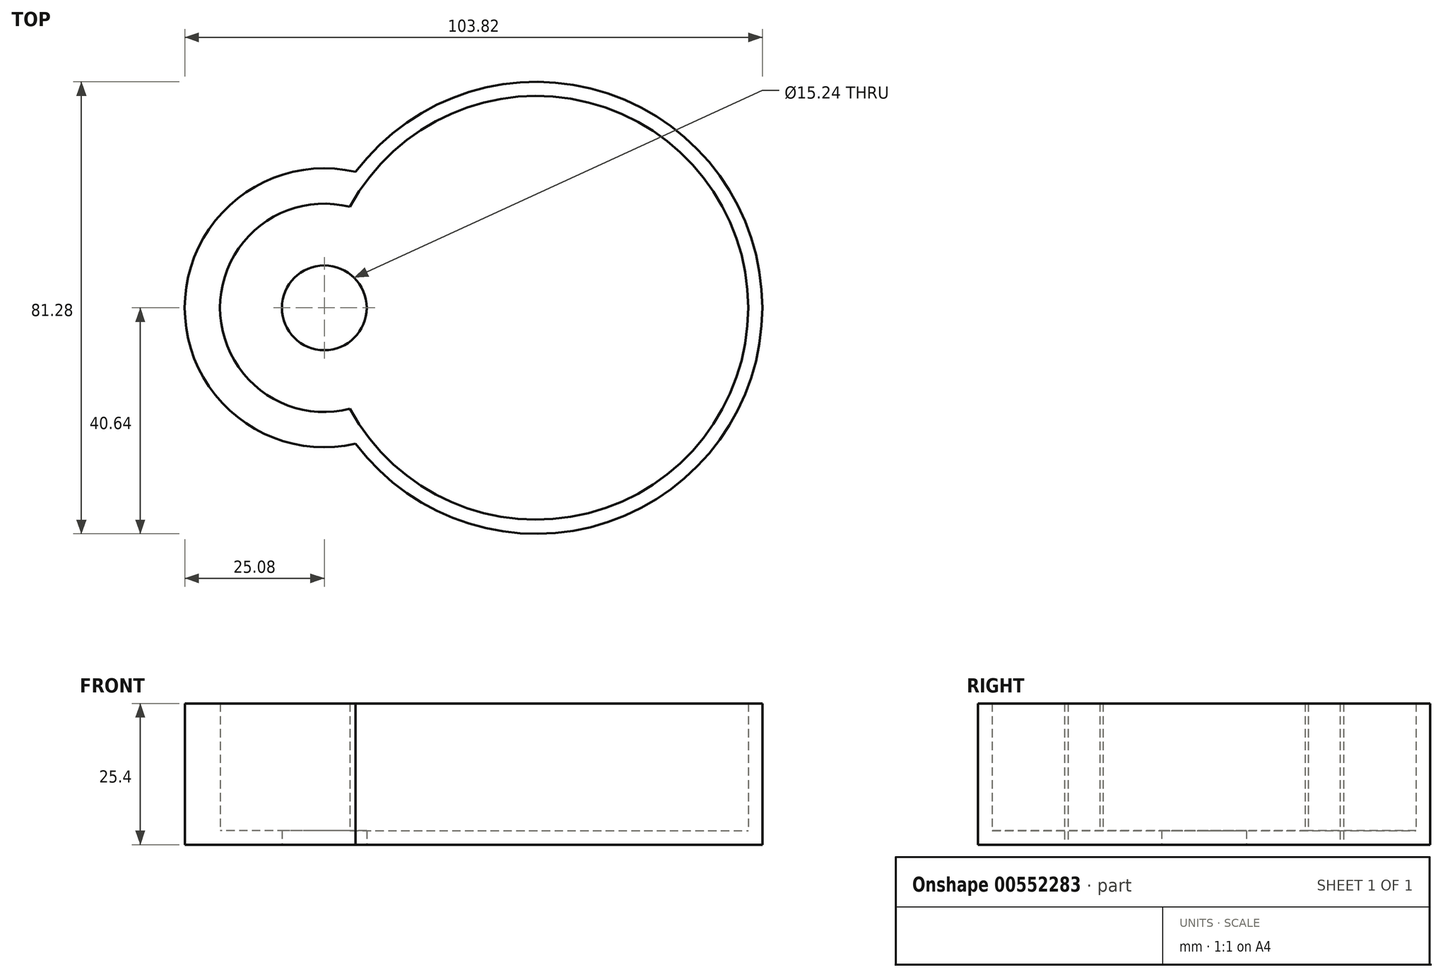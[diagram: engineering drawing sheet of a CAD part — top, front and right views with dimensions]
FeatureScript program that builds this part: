
annotation { "Feature Type Name" : "Feature", "Feature Type Description" : "" }
export const myFeature = defineFeature(function(context is Context, id is Id, definition is map)
    precondition{}
    {
        {
            var Q0;
            Q0=qCreatedBy(makeId("Top.planeOp"),FACE);
            var sketch = newSketch(context, id + "F0", { "sketchPlane" : qUnion([Q0])});
            skCircle(sketch, "E0", {"center": v(0, 0) * mm, "radius": 18.73 * mm});
            skCircle(sketch, "E1.0", {"center": v(0, 0) * mm, "radius": 25.08 * mm});
            skCircle(sketch, "E2", {"center": v(0, 0) * mm, "radius": 7.62 * mm});
            skCircle(sketch, "E3", {"center": v(38.1, 0) * mm, "radius": 6.35 * mm});
            skCircle(sketch, "E4", {"center": v(38.1, 0) * mm, "radius": 38.1 * mm});
            skCircle(sketch, "E5.0", {"center": v(38.1, 0) * mm, "radius": 40.64 * mm});
            skSolve(sketch);
        }
        {
            var Q0;
            Q0 = qSketchRegion(id + "F0", true);
            var Q1;
            {var subQ0=sQuery(id+"F0.wireOp",EDGE,"E5.0");var subQ1=sQuery(id+"F0.wireOp",EDGE,"E0");var subQ2=makeQuery(id+"F0.imprint","INTERSECT",VERTEX,{"disambiguationData":[OD(0.0)],"derivedFrom":[subQ1,subQ0]});Q1=makeQuery(id+"F0.imprint","IMPRINT",FACE,{"disambiguationData":[TD([[makeQuery(id+"F0.imprint","IMPRINT",EDGE,{"disambiguationData":[TD([[subQ2,-1.0]])],"derivedFrom":subQ1}),1.0]])]});}
            var Q2;
            {var subQ0=sQuery(id+"F0.wireOp",EDGE,"E5.0");var subQ1=sQuery(id+"F0.wireOp",EDGE,"E0");var subQ2=makeQuery(id+"F0.imprint","INTERSECT",VERTEX,{"disambiguationData":[OD(0.0)],"derivedFrom":[subQ1,subQ0]});Q2=makeQuery(id+"F0.imprint","IMPRINT",FACE,{"disambiguationData":[TD([[makeQuery(id+"F0.imprint","IMPRINT",EDGE,{"disambiguationData":[TD([[subQ2,1.0]])],"derivedFrom":subQ1}),1.0]])]});}
            var Q3;
            {var subQ0=sQuery(id+"F0.wireOp",EDGE,"E4");var subQ1=sQuery(id+"F0.wireOp",EDGE,"E0");var subQ2=makeQuery(id+"F0.imprint","INTERSECT",VERTEX,{"disambiguationData":[OD(0.0)],"derivedFrom":[subQ1,subQ0]});Q3=makeQuery(id+"F0.imprint","IMPRINT",FACE,{"disambiguationData":[TD([[makeQuery(id+"F0.imprint","IMPRINT",EDGE,{"disambiguationData":[TD([[subQ2,1.0]])],"derivedFrom":subQ1}),1.0]])]});}
            var Q4;
            {var subQ0=sQuery(id+"F0.wireOp",EDGE,"E5.0");var subQ1=sQuery(id+"F0.wireOp",EDGE,"E0");var subQ2=makeQuery(id+"F0.imprint","INTERSECT",VERTEX,{"disambiguationData":[OD(1.0)],"derivedFrom":[subQ1,subQ0]});Q4=makeQuery(id+"F0.imprint","IMPRINT",FACE,{"disambiguationData":[TD([[makeQuery(id+"F0.imprint","IMPRINT",EDGE,{"disambiguationData":[TD([[subQ2,-1.0]])],"derivedFrom":subQ1}),1.0]])]});}
            var Q5;
            {var subQ0=sQuery(id+"F0.wireOp",EDGE,"E4");var subQ1=sQuery(id+"F0.wireOp",EDGE,"E0");var subQ2=makeQuery(id+"F0.imprint","INTERSECT",VERTEX,{"disambiguationData":[OD(0.0)],"derivedFrom":[subQ1,subQ0]});Q5=makeQuery(id+"F0.imprint","IMPRINT",FACE,{"disambiguationData":[TD([[makeQuery(id+"F0.imprint","IMPRINT",EDGE,{"disambiguationData":[TD([[subQ2,1.0]])],"derivedFrom":subQ1}),-1.0]])]});}
            var Q6;
            Q6=makeQuery(id+"F0.imprint","IMPRINT",FACE,{"disambiguationData":[TD([[makeQuery(id+"F0.imprint","IMPRINT",EDGE,{"derivedFrom":sQuery(id+"F0.wireOp",EDGE,"E3")}),-1.0]])]});
            var Q7;
            Q7=makeQuery(id+"F0.imprint","IMPRINT",FACE,{"disambiguationData":[TD([[makeQuery(id+"F0.imprint","IMPRINT",EDGE,{"derivedFrom":sQuery(id+"F0.wireOp",EDGE,"E3")}),1.0]])]});
            extrude(context, id + "F1", {"entities" : qUnion([Q0, Q1, Q2, Q3, Q4, Q5, Q6, Q7]), "depth" : 2.54 * mm, "offsetDistance" : 25.4 * mm});
        }
        {
            var Q0;
            {var subQ0=sQuery(id+"F0.wireOp",EDGE,"E5.0");var subQ1=sQuery(id+"F0.wireOp",EDGE,"E1.0");var subQ2=makeQuery(id+"F0.imprint","INTERSECT",VERTEX,{"disambiguationData":[OD(0.0)],"derivedFrom":[subQ1,subQ0]});Q0=makeQuery(id+"F0.imprint","IMPRINT",FACE,{"disambiguationData":[TD([[makeQuery(id+"F0.imprint","IMPRINT",EDGE,{"disambiguationData":[TD([[subQ2,1.0]])],"derivedFrom":subQ1}),-1.0]])]});}
            var Q1;
            {var subQ0=sQuery(id+"F0.wireOp",EDGE,"E5.0");var subQ1=sQuery(id+"F0.wireOp",EDGE,"E0");var subQ2=makeQuery(id+"F0.imprint","INTERSECT",VERTEX,{"disambiguationData":[OD(0.0)],"derivedFrom":[subQ1,subQ0]});Q1=makeQuery(id+"F0.imprint","IMPRINT",FACE,{"disambiguationData":[TD([[makeQuery(id+"F0.imprint","IMPRINT",EDGE,{"disambiguationData":[TD([[subQ2,1.0]])],"derivedFrom":subQ1}),-1.0]])]});}
            var Q2;
            {var subQ0=sQuery(id+"F0.wireOp",EDGE,"E5.0");var subQ1=sQuery(id+"F0.wireOp",EDGE,"E0");var subQ2=makeQuery(id+"F0.imprint","INTERSECT",VERTEX,{"disambiguationData":[OD(0.0)],"derivedFrom":[subQ1,subQ0]});Q2=makeQuery(id+"F0.imprint","IMPRINT",FACE,{"disambiguationData":[TD([[makeQuery(id+"F0.imprint","IMPRINT",EDGE,{"disambiguationData":[TD([[subQ2,-1.0]])],"derivedFrom":subQ1}),-1.0]])]});}
            var Q3;
            {var subQ0=sQuery(id+"F0.wireOp",EDGE,"E5.0");var subQ1=sQuery(id+"F0.wireOp",EDGE,"E0");var subQ2=makeQuery(id+"F0.imprint","INTERSECT",VERTEX,{"disambiguationData":[OD(1.0)],"derivedFrom":[subQ1,subQ0]});Q3=makeQuery(id+"F0.imprint","IMPRINT",FACE,{"disambiguationData":[TD([[makeQuery(id+"F0.imprint","IMPRINT",EDGE,{"disambiguationData":[TD([[subQ2,-1.0]])],"derivedFrom":subQ1}),-1.0]])]});}
            extrude(context, id + "F2", {"entities" : qUnion([Q0, Q1, Q2, Q3]), "operationType" : NewBodyOperationType.ADD, "depth" : 25.4 * mm, "offsetDistance" : 25.4 * mm});
        }
    });
